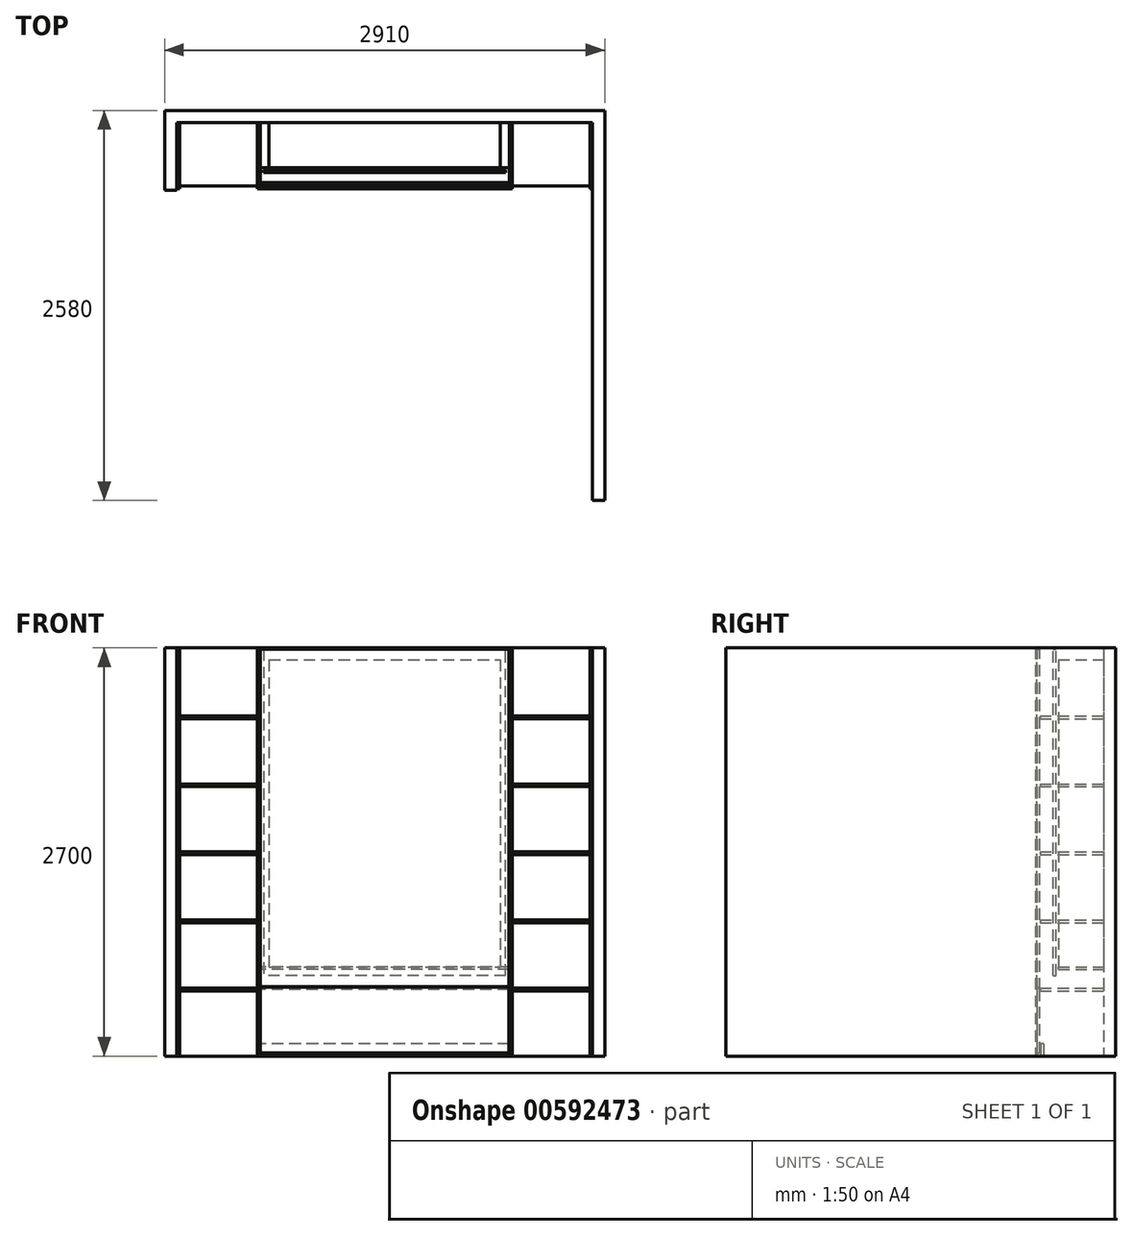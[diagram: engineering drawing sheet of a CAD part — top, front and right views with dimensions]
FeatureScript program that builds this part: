
annotation { "Feature Type Name" : "Feature", "Feature Type Description" : "" }
export const myFeature = defineFeature(function(context is Context, id is Id, definition is map)
    precondition{}
    {
        {
            var Q0;
            Q0=qCreatedBy(makeId("Top.planeOp"),FACE);
            var sketch = newSketch(context, id + "F0", { "sketchPlane" : qUnion([Q0])});
            skLineSegment(sketch, "E0", {"start": v(-1375, -450) * mm, "end": v(-1375, 0) * mm});
            skLineSegment(sketch, "E1", {"start": v(-1375, 0) * mm, "end": v(1375, 0) * mm});
            skLineSegment(sketch, "E2", {"start": v(1375, 0) * mm, "end": v(1375, -2500) * mm});
            skLineSegment(sketch, "E3", {"start": v(-1375, -450) * mm, "end": v(-1455, -450) * mm});
            skLineSegment(sketch, "E4", {"start": v(-1455, -450) * mm, "end": v(-1455, 80) * mm});
            skLineSegment(sketch, "E5", {"start": v(-1455, 80) * mm, "end": v(1455, 80) * mm});
            skLineSegment(sketch, "E6", {"start": v(1455, 80) * mm, "end": v(1455, -2500) * mm});
            skLineSegment(sketch, "E7", {"start": v(1455, -2500) * mm, "end": v(1375, -2500) * mm});
            skSolve(sketch);
        }
        {
            var Q0;
            Q0 = qSketchRegion(id + "F0", true);
            extrude(context, id + "F1", {"entities" : qUnion([Q0]), "depth" : 2700 * mm, "offsetDistance" : 25 * mm});
        }
        {
            var Q0;
            Q0=qCreatedBy(makeId("Front.planeOp"),FACE);
            var sketch = newSketch(context, id + "F2", { "sketchPlane" : qUnion([Q0])});
            skLineSegment(sketch, "E8.bottom", {"start": v(-765, 2620) * mm, "end": v(765, 2620) * mm});
            skLineSegment(sketch, "E8.top", {"start": v(-765, 590) * mm, "end": v(765, 590) * mm});
            skLineSegment(sketch, "E8.left", {"start": v(-765, 2620) * mm, "end": v(-765, 590) * mm});
            skLineSegment(sketch, "E8.right", {"start": v(765, 2620) * mm, "end": v(765, 590) * mm});
            skLineSegment(sketch, "E9", {"start": v(0, 0) * mm, "end": v(0, 590) * mm, "construction": true});
            skLineSegment(sketch, "E10", {"start": v(-765, 2620) * mm, "end": v(-1365, 2620) * mm, "construction": true});
            skSolve(sketch);
        }
        {
            var Q0;
            Q0 = qSketchRegion(id + "F2", true);
            extrude(context, id + "F3", {"entities" : qUnion([Q0]), "depth" : 300 * mm, "offsetDistance" : 25 * mm});
        }
        {
            var Q0;
            Q0=qCreatedBy(makeId("Front.planeOp"),FACE);
            var sketch = newSketch(context, id + "F4", { "sketchPlane" : qUnion([Q0])});
            skLineSegment(sketch, "E11.bottom", {"start": v(-843, 2700) * mm, "end": v(-825, 2700) * mm});
            skLineSegment(sketch, "E11.top", {"start": v(-843, 0) * mm, "end": v(-825, 0) * mm});
            skLineSegment(sketch, "E11.left", {"start": v(-843, 2700) * mm, "end": v(-843, 0) * mm});
            skLineSegment(sketch, "E11.right", {"start": v(-825, 2700) * mm, "end": v(-825, 0) * mm});
            skSolve(sketch);
        }
        {
            var Q0;
            Q0 = qSketchRegion(id + "F4", true);
            extrude(context, id + "F5", {"entities" : qUnion([Q0]), "depth" : 440 * mm, "offsetDistance" : 25 * mm});
        }
        {
            var Q0;
            Q0=qCreatedBy(makeId("Front.planeOp"),FACE);
            var sketch = newSketch(context, id + "F6", { "sketchPlane" : qUnion([Q0])});
            skLineSegment(sketch, "E12.bottom", {"start": v(-1357, 2700) * mm, "end": v(-1375, 2700) * mm});
            skLineSegment(sketch, "E12.top", {"start": v(-1357, 0) * mm, "end": v(-1375, 0) * mm});
            skLineSegment(sketch, "E12.left", {"start": v(-1357, 2700) * mm, "end": v(-1357, 0) * mm});
            skLineSegment(sketch, "E12.right", {"start": v(-1375, 2700) * mm, "end": v(-1375, 0) * mm});
            skSolve(sketch);
        }
        {
            var Q0;
            Q0 = qSketchRegion(id + "F6", true);
            extrude(context, id + "F7", {"entities" : qUnion([Q0]), "depth" : 440 * mm, "offsetDistance" : 25 * mm});
        }
        {
            var Q0;
            Q0=qCreatedBy(makeId("Front.planeOp"),FACE);
            var sketch = newSketch(context, id + "F8", { "sketchPlane" : qUnion([Q0])});
            skLineSegment(sketch, "E13", {"start": v(-1357, 2700) * mm, "end": v(-843, 2700) * mm, "construction": true});
            skLineSegment(sketch, "E14.bottom", {"start": v(-1357, 2250) * mm, "end": v(-843, 2250) * mm});
            skLineSegment(sketch, "E14.top", {"start": v(-1357, 2232) * mm, "end": v(-843, 2232) * mm});
            skLineSegment(sketch, "E14.left", {"start": v(-1357, 2250) * mm, "end": v(-1357, 2232) * mm});
            skLineSegment(sketch, "E14.right", {"start": v(-843, 2250) * mm, "end": v(-843, 2232) * mm});
            skLineSegment(sketch, "E15.0.1.0", {"start": v(-1357, 1800) * mm, "end": v(-843, 1800) * mm});
            skLineSegment(sketch, "E15.0.1.1", {"start": v(-1357, 1782) * mm, "end": v(-843, 1782) * mm});
            skLineSegment(sketch, "E15.0.1.2", {"start": v(-843, 1800) * mm, "end": v(-843, 1782) * mm});
            skLineSegment(sketch, "E15.0.1.3", {"start": v(-1357, 1800) * mm, "end": v(-1357, 1782) * mm});
            skLineSegment(sketch, "E15.0.2.0", {"start": v(-1357, 1350) * mm, "end": v(-843, 1350) * mm});
            skLineSegment(sketch, "E15.0.2.1", {"start": v(-1357, 1332) * mm, "end": v(-843, 1332) * mm});
            skLineSegment(sketch, "E15.0.2.2", {"start": v(-843, 1350) * mm, "end": v(-843, 1332) * mm});
            skLineSegment(sketch, "E15.0.2.3", {"start": v(-1357, 1350) * mm, "end": v(-1357, 1332) * mm});
            skLineSegment(sketch, "E15.0.3.0", {"start": v(-1357, 900) * mm, "end": v(-843, 900) * mm});
            skLineSegment(sketch, "E15.0.3.1", {"start": v(-1357, 882) * mm, "end": v(-843, 882) * mm});
            skLineSegment(sketch, "E15.0.3.2", {"start": v(-843, 900) * mm, "end": v(-843, 882) * mm});
            skLineSegment(sketch, "E15.0.3.3", {"start": v(-1357, 900) * mm, "end": v(-1357, 882) * mm});
            skLineSegment(sketch, "E15.direction1", {"start": v(-1357, 2232) * mm, "end": v(-1332, 2232) * mm, "construction": true});
            skLineSegment(sketch, "E15.direction2", {"start": v(-1357, 2232) * mm, "end": v(-1357, 1782) * mm, "construction": true});
            skLineSegment(sketch, "E16.0.0.4", {"start": v(-1357, 450) * mm, "end": v(-843, 450) * mm});
            skLineSegment(sketch, "E16.3.0.4", {"start": v(-1357, 432) * mm, "end": v(-843, 432) * mm});
            skLineSegment(sketch, "E16.6.0.4", {"start": v(-843, 450) * mm, "end": v(-843, 432) * mm});
            skLineSegment(sketch, "E16.9.0.4", {"start": v(-1357, 450) * mm, "end": v(-1357, 432) * mm});
            skSolve(sketch);
        }
        {
            var Q0;
            Q0 = qSketchRegion(id + "F8", true);
            extrude(context, id + "F9", {"entities" : qUnion([Q0]), "depth" : 420 * mm, "offsetDistance" : 25 * mm});
        }
        {
            var Q0;
            Q0=makeQuery(id+"F7.opExtrude","SWEPT_BODY",BODY,{"disambiguationData":[OSD([sQuery(id+"F6.wireOp",EDGE,"E12.bottom"),sQuery(id+"F6.wireOp",EDGE,"E12.top"),sQuery(id+"F6.wireOp",EDGE,"E12.left"),sQuery(id+"F6.wireOp",EDGE,"E12.right")])]});
            var Q1;
            Q1=makeQuery(id+"F5.opExtrude","SWEPT_BODY",BODY,{"disambiguationData":[OSD([sQuery(id+"F4.wireOp",EDGE,"E11.bottom"),sQuery(id+"F4.wireOp",EDGE,"E11.top"),sQuery(id+"F4.wireOp",EDGE,"E11.left"),sQuery(id+"F4.wireOp",EDGE,"E11.right")])]});
            var Q2;
            Q2=makeQuery(id+"F9.opExtrude","SWEPT_BODY",BODY,{"disambiguationData":[OSD([sQuery(id+"F8.wireOp",EDGE,"E14.bottom"),sQuery(id+"F8.wireOp",EDGE,"E14.top"),sQuery(id+"F8.wireOp",EDGE,"E14.left"),sQuery(id+"F8.wireOp",EDGE,"E14.right")])]});
            var Q3;
            Q3=makeQuery(id+"F9.opExtrude","SWEPT_BODY",BODY,{"disambiguationData":[OSD([sQuery(id+"F8.wireOp",EDGE,"E15.0.1.0"),sQuery(id+"F8.wireOp",EDGE,"E15.0.1.1"),sQuery(id+"F8.wireOp",EDGE,"E15.0.1.2"),sQuery(id+"F8.wireOp",EDGE,"E15.0.1.3")])]});
            var Q4;
            Q4=makeQuery(id+"F9.opExtrude","SWEPT_BODY",BODY,{"disambiguationData":[OSD([sQuery(id+"F8.wireOp",EDGE,"E15.0.2.0"),sQuery(id+"F8.wireOp",EDGE,"E15.0.2.1"),sQuery(id+"F8.wireOp",EDGE,"E15.0.2.2"),sQuery(id+"F8.wireOp",EDGE,"E15.0.2.3")])]});
            var Q5;
            Q5=makeQuery(id+"F9.opExtrude","SWEPT_BODY",BODY,{"disambiguationData":[OSD([sQuery(id+"F8.wireOp",EDGE,"E15.0.3.0"),sQuery(id+"F8.wireOp",EDGE,"E15.0.3.1"),sQuery(id+"F8.wireOp",EDGE,"E15.0.3.2"),sQuery(id+"F8.wireOp",EDGE,"E15.0.3.3")])]});
            var Q6;
            Q6=makeQuery(id+"F9.opExtrude","SWEPT_BODY",BODY,{"disambiguationData":[OSD([sQuery(id+"F8.wireOp",EDGE,"E16.0.0.4"),sQuery(id+"F8.wireOp",EDGE,"E16.3.0.4"),sQuery(id+"F8.wireOp",EDGE,"E16.6.0.4"),sQuery(id+"F8.wireOp",EDGE,"E16.9.0.4")])]});
            var Q7;
            Q7=qCreatedBy(makeId("Right.planeOp"),FACE);
            mirror(context, id + "F10", {"entities" : qUnion([Q0, Q1, Q2, Q3, Q4, Q5, Q6]), "mirrorPlane" : qUnion([Q7])});
        }
        {
            var Q0;
            Q0=qCreatedBy(makeId("Right.planeOp"),FACE);
            var sketch = newSketch(context, id + "F11", { "sketchPlane" : qUnion([Q0])});
            skLineSegment(sketch, "E17.bottom", {"start": v(-422, 2690) * mm, "end": v(-440, 2690) * mm});
            skLineSegment(sketch, "E17.left", {"start": v(-422, 2690) * mm, "end": v(-422, 442) * mm});
            skLineSegment(sketch, "E17.right", {"start": v(-440, 2690) * mm, "end": v(-440, 460) * mm});
            skLineSegment(sketch, "E18", {"start": v(-440, 460) * mm, "end": v(-422, 442) * mm});
            skSolve(sketch);
        }
        {
            var Q0;
            Q0 = qSketchRegion(id + "F11", true);
            var Q1;
            Q1=makeQuery(id+"F10.opPattern","COPY",FACE,{"derivedFrom":makeQuery(id+"F5.opExtrude","SWEPT_FACE",FACE,{"disambiguationData":[OSD([sQuery(id+"F4.wireOp",EDGE,"E11.right")])]}),"instanceName":"1"});
            extrude(context, id + "F12", {"entities" : qUnion([Q0]), "endBound" : BoundingType.UP_TO_SURFACE, "depth" : 25 * mm, "endBoundEntityFace" : qUnion([Q1]), "hasOffset" : true, "offsetDistance" : 3 * mm, "hasSecondDirection" : true, "secondDirectionBound" : BoundingType.UP_TO_NEXT, "secondDirectionOppositeDirection" : true, "secondDirectionDepth" : 25 * mm, "hasSecondDirectionOffset" : true, "secondDirectionOffsetDistance" : 3 * mm});
        }
        {
            var Q0;
            Q0=qCreatedBy(makeId("Right.planeOp"),FACE);
            var sketch = newSketch(context, id + "F13", { "sketchPlane" : qUnion([Q0])});
            skLineSegment(sketch, "E19.bottom", {"start": v(0, 590) * mm, "end": v(-300, 590) * mm});
            skLineSegment(sketch, "E19.top", {"start": v(0, 572) * mm, "end": v(-300, 572) * mm});
            skLineSegment(sketch, "E19.left", {"start": v(0, 590) * mm, "end": v(0, 572) * mm});
            skLineSegment(sketch, "E19.right", {"start": v(-300, 590) * mm, "end": v(-300, 572) * mm});
            skSolve(sketch);
        }
        {
            var Q0;
            Q0 = qSketchRegion(id + "F13", true);
            extrude(context, id + "F14", {"entities" : qUnion([Q0]), "endBound" : BoundingType.UP_TO_NEXT, "depth" : 25 * mm, "offsetDistance" : 25 * mm, "hasSecondDirection" : true, "secondDirectionBound" : BoundingType.UP_TO_NEXT, "secondDirectionOppositeDirection" : true, "secondDirectionDepth" : 25 * mm});
        }
        {
            var Q0;
            Q0=qCreatedBy(makeId("Right.planeOp"),FACE);
            var sketch = newSketch(context, id + "F15", { "sketchPlane" : qUnion([Q0])});
            skLineSegment(sketch, "E20.left", {"start": v(-422, 439) * mm, "end": v(-422, 20) * mm});
            skLineSegment(sketch, "E20.right", {"start": v(-440, 457) * mm, "end": v(-440, 20) * mm});
            skLineSegment(sketch, "E21", {"start": v(-422, 20) * mm, "end": v(-440, 20) * mm});
            skLineSegment(sketch, "E22", {"start": v(-440, 457) * mm, "end": v(-422, 439) * mm});
            skSolve(sketch);
        }
        {
            var Q0;
            Q0 = qSketchRegion(id + "F15", true);
            extrude(context, id + "F16", {"entities" : qUnion([Q0]), "endBound" : BoundingType.UP_TO_NEXT, "depth" : 25 * mm, "hasOffset" : true, "offsetDistance" : 3 * mm, "hasSecondDirection" : true, "secondDirectionBound" : BoundingType.UP_TO_NEXT, "secondDirectionOppositeDirection" : true, "secondDirectionDepth" : 25 * mm, "hasSecondDirectionOffset" : true, "secondDirectionOffsetDistance" : 3 * mm});
        }
        {
            var Q0;
            Q0=qCreatedBy(makeId("Right.planeOp"),FACE);
            var sketch = newSketch(context, id + "F17", { "sketchPlane" : qUnion([Q0])});
            skLineSegment(sketch, "E23.bottom", {"start": v(-416, 0) * mm, "end": v(-398, 0) * mm});
            skLineSegment(sketch, "E23.top", {"start": v(-416, 80) * mm, "end": v(-398, 80) * mm});
            skLineSegment(sketch, "E23.left", {"start": v(-416, 0) * mm, "end": v(-416, 80) * mm});
            skLineSegment(sketch, "E23.right", {"start": v(-398, 0) * mm, "end": v(-398, 80) * mm});
            skSolve(sketch);
        }
        {
            var Q0;
            Q0 = qSketchRegion(id + "F17", true);
            extrude(context, id + "F18", {"entities" : qUnion([Q0]), "endBound" : BoundingType.UP_TO_NEXT, "depth" : 25 * mm, "offsetDistance" : 25 * mm, "hasSecondDirection" : true, "secondDirectionBound" : BoundingType.UP_TO_NEXT, "secondDirectionOppositeDirection" : true, "secondDirectionDepth" : 25 * mm});
        }
        {
            var Q0;
            Q0=qCreatedBy(makeId("Right.planeOp"),FACE);
            var sketch = newSketch(context, id + "F19", { "sketchPlane" : qUnion([Q0])});
            skLineSegment(sketch, "E24.bottom", {"start": v(-314, 2690) * mm, "end": v(-332, 2690) * mm});
            skLineSegment(sketch, "E24.top", {"start": v(-314, 532) * mm, "end": v(-332, 532) * mm});
            skLineSegment(sketch, "E24.left", {"start": v(-314, 2690) * mm, "end": v(-314, 532) * mm});
            skLineSegment(sketch, "E24.right", {"start": v(-332, 2690) * mm, "end": v(-332, 532) * mm});
            skSolve(sketch);
        }
        {
            var Q0;
            Q0 = qSketchRegion(id + "F19", true);
            extrude(context, id + "F20", {"entities" : qUnion([Q0]), "endBound" : BoundingType.UP_TO_NEXT, "depth" : 25 * mm, "hasOffset" : true, "offsetDistance" : 25 * mm, "hasSecondDirection" : true, "secondDirectionBound" : BoundingType.UP_TO_NEXT, "secondDirectionOppositeDirection" : true, "secondDirectionDepth" : 25 * mm, "hasSecondDirectionOffset" : true, "secondDirectionOffsetDistance" : 25 * mm});
        }
    });
